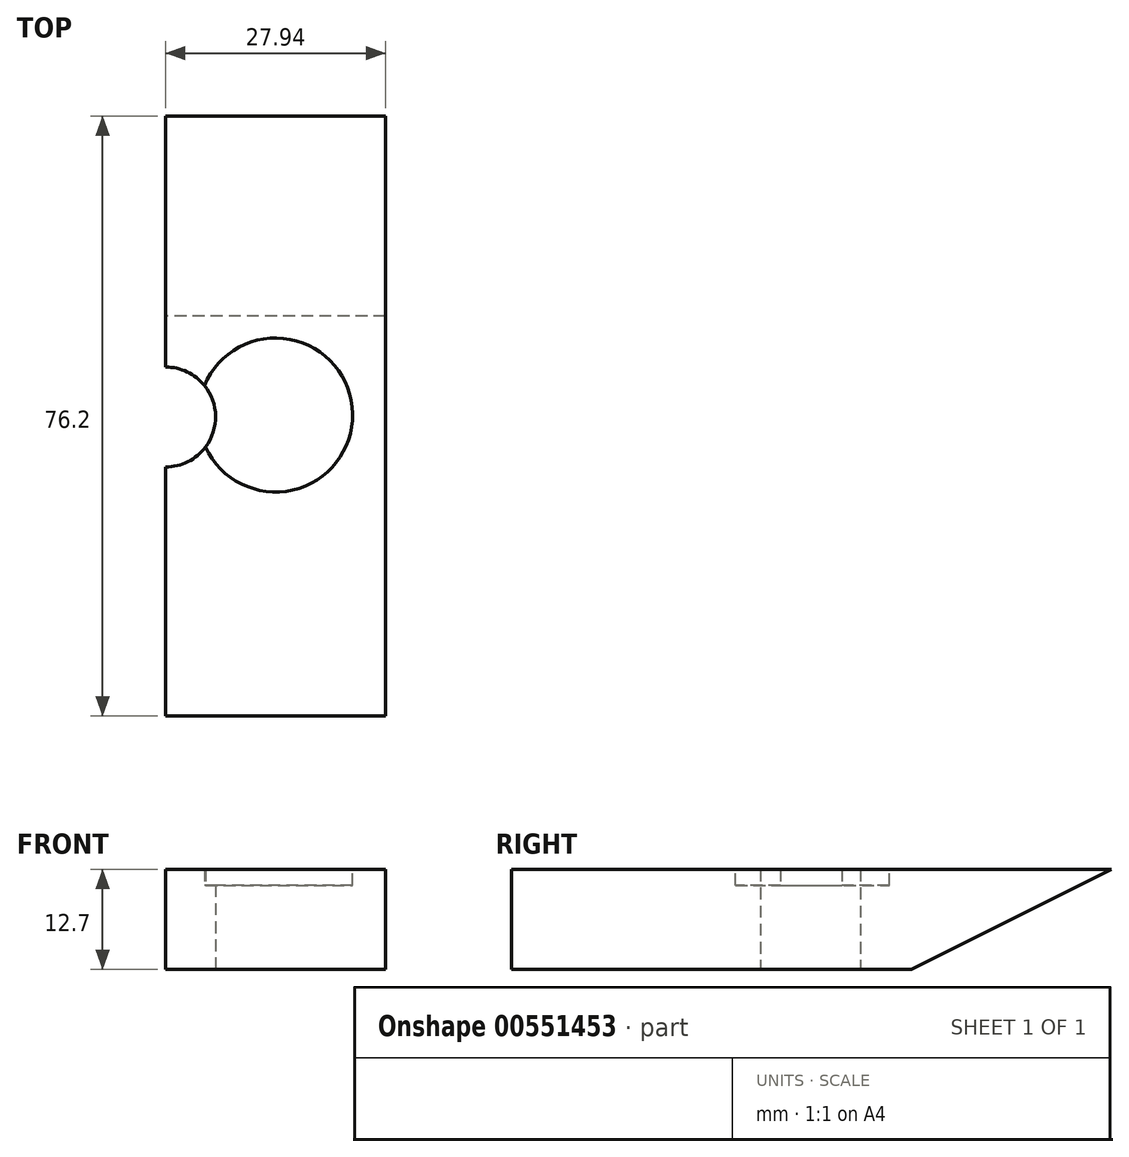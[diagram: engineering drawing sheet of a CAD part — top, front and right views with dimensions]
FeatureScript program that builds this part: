
annotation { "Feature Type Name" : "Feature", "Feature Type Description" : "" }
export const myFeature = defineFeature(function(context is Context, id is Id, definition is map)
    precondition{}
    {
        {
            var Q0;
            Q0=qCreatedBy(makeId("Right.planeOp"),FACE);
            var sketch = newSketch(context, id + "F0", { "sketchPlane" : qUnion([Q0])});
            skLineSegment(sketch, "E0", {"start": v(0, 0) * mm, "end": v(0, 12.7) * mm});
            skLineSegment(sketch, "E1", {"start": v(0, 12.7) * mm, "end": v(76.2, 12.7) * mm});
            skLineSegment(sketch, "E2", {"start": v(76.2, 12.7) * mm, "end": v(50.8, 0) * mm});
            skLineSegment(sketch, "E3", {"start": v(50.8, 0) * mm, "end": v(0, 0) * mm});
            skSolve(sketch);
        }
        {
            var Q0;
            Q0=qSketchRegion(id+"F0",true);
            extrude(context, id + "F1", {"entities" : qUnion([Q0]), "depth" : 27.94 * mm, "offsetDistance" : 25.4 * mm});
        }
        {
            var Q0;
            Q0=makeQuery(id+"F1.opExtrude","SWEPT_FACE",FACE,{"disambiguationData":[OSD([sQuery(id+"F0.wireOp",EDGE,"E1")])]});
            var sketch = newSketch(context, id + "F2", { "sketchPlane" : qUnion([Q0])});
            skCircle(sketch, "E4", {"center": v(13.97, 38.23) * mm, "radius": 9.78 * mm});
            skLineSegment(sketch, "E5", {"start": v(13.97, 76.2) * mm, "end": v(13.97, 48) * mm, "construction": true});
            skLineSegment(sketch, "E6", {"start": v(13.97, 38.23) * mm, "end": v(0, 38.23) * mm, "construction": true});
            skLineSegment(sketch, "E7", {"start": v(0, 38.23) * mm, "end": v(0, 76.2) * mm, "construction": true});
            skSolve(sketch);
        }
        {
            var Q0;
            Q0=qSketchRegion(id+"F2",true);
            extrude(context, id + "F3", {"entities" : qUnion([Q0]), "operationType" : NewBodyOperationType.REMOVE, "oppositeDirection" : true, "depth" : 2 * mm, "offsetDistance" : 25.4 * mm});
        }
        {
            var Q0;
            Q0=qCreatedBy(makeId("Top.planeOp"),FACE);
            var sketch = newSketch(context, id + "F4", { "sketchPlane" : qUnion([Q0])});
            skLineSegment(sketch, "E8", {"start": v(0, 0) * mm, "end": v(0, 75.95) * mm});
            skLineSegment(sketch, "E9", {"start": v(14.07, 37.97) * mm, "end": v(0, 37.97) * mm});
            skPoint(sketch, "E9.startSnap0", {"position": v(0, 37.97) * mm});
            skCircle(sketch, "E10", {"center": v(0, 37.97) * mm, "radius": 6.35 * mm});
            skLineSegment(sketch, "E11", {"start": v(0, 75.95) * mm, "end": v(0, 37.97) * mm, "construction": true});
            skSolve(sketch);
        }
        {
            var Q0;
            Q0=qSketchRegion(id+"F4",true);
            extrude(context, id + "F5", {"entities" : qUnion([Q0]), "operationType" : NewBodyOperationType.REMOVE, "depth" : 25.4 * mm, "offsetDistance" : 25.4 * mm});
        }
    });
